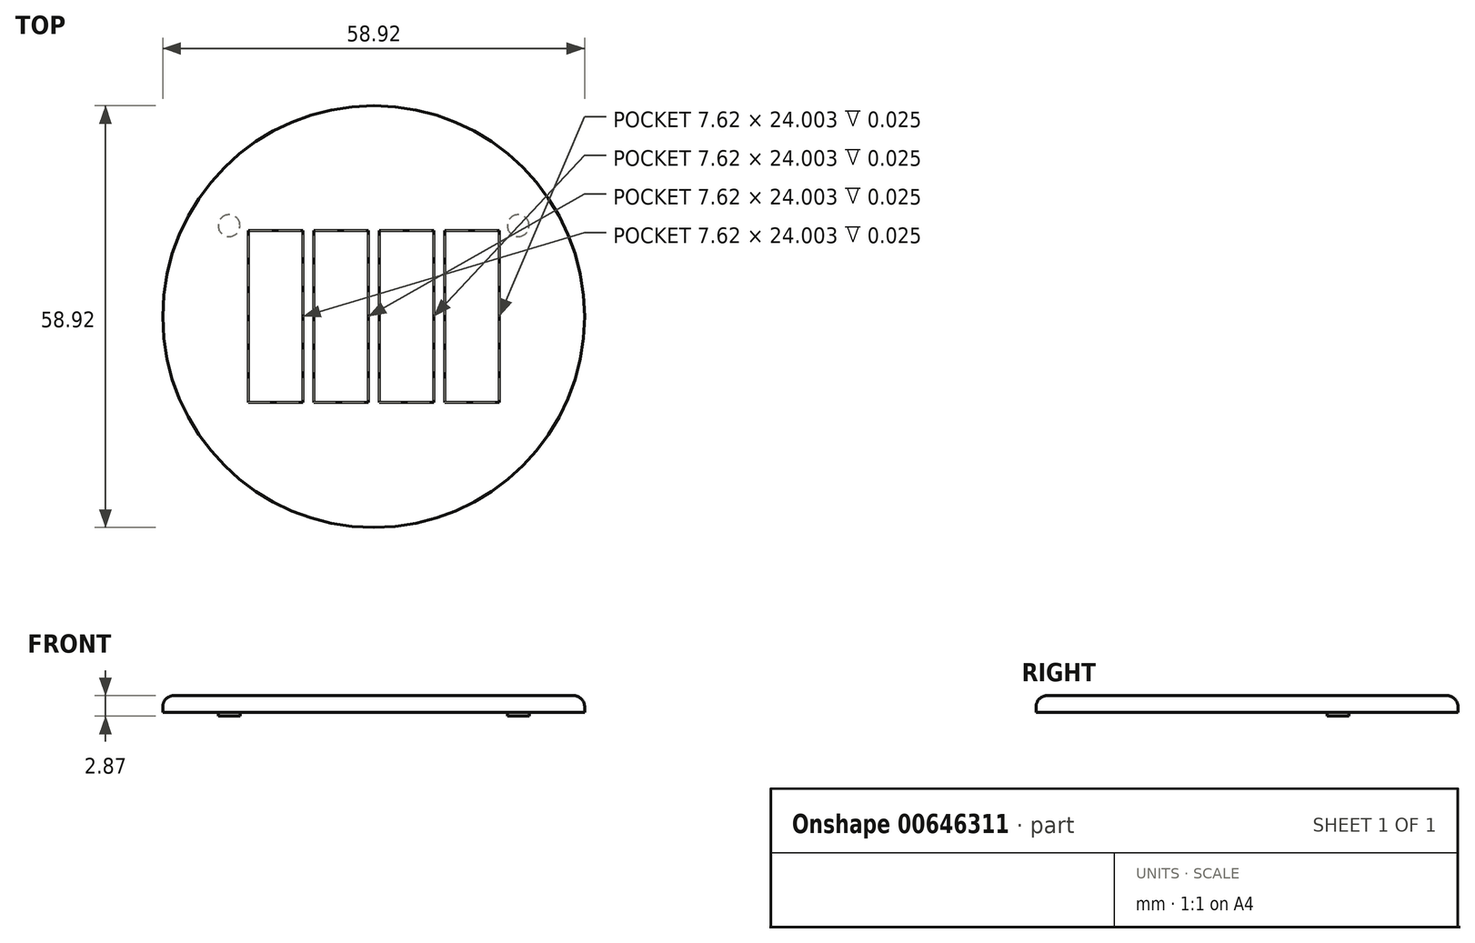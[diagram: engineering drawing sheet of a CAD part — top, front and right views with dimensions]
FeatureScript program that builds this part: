
annotation { "Feature Type Name" : "Feature", "Feature Type Description" : "" }
export const myFeature = defineFeature(function(context is Context, id is Id, definition is map)
    precondition{}
    {
        {
            var Q0;
            Q0=qCreatedBy(makeId("Top.planeOp"),FACE);
            var sketch = newSketch(context, id + "F0", { "sketchPlane" : qUnion([Q0])});
            skCircle(sketch, "E0", {"center": v(0, 0) * mm, "radius": 29.46 * mm});
            skSolve(sketch);
        }
        {
            var Q0;
            Q0 = qSketchRegion(id + "F0", true);
            extrude(context, id + "F1", {"entities" : qUnion([Q0]), "depth" : 2.36 * mm, "offsetDistance" : 25.4 * mm});
        }
        {
            var Q0;
            Q0=makeQuery(id+"F1.opExtrude","CAP_EDGE",EDGE,{"disambiguationData":[OSD([sQuery(id+"F0.wireOp",EDGE,"E0")])],"isStart":false});
            fillet(context, id + "F2", {"entities" : qUnion([Q0]), "radius" : 1.52 * mm, "tangentPropagation" : true, "allowEdgeOverflow" : false});
        }
        {
            var Q0;
            Q0=makeQuery(id+"F1.opExtrude","CAP_FACE",FACE,{"disambiguationData":[OSD([sQuery(id+"F0.wireOp",EDGE,"E0")])],"isStart":false});
            var sketch = newSketch(context, id + "F3", { "sketchPlane" : qUnion([Q0])});
            skLineSegment(sketch, "E1.bottom", {"start": v(-17.53, 12) * mm, "end": v(-9.9, 12) * mm});
            skLineSegment(sketch, "E1.top", {"start": v(-17.53, -12) * mm, "end": v(-9.9, -12) * mm});
            skLineSegment(sketch, "E1.left", {"start": v(-17.53, 12) * mm, "end": v(-17.53, -12) * mm});
            skLineSegment(sketch, "E1.right", {"start": v(-9.9, 12) * mm, "end": v(-9.9, -12) * mm});
            skLineSegment(sketch, "E2.1.0.0", {"start": v(-8.38, 12) * mm, "end": v(-0.76, 12) * mm});
            skLineSegment(sketch, "E2.1.0.1", {"start": v(-8.38, -12) * mm, "end": v(-0.76, -12) * mm});
            skLineSegment(sketch, "E2.1.0.2", {"start": v(-8.38, 12) * mm, "end": v(-8.38, -12) * mm});
            skLineSegment(sketch, "E2.1.0.3", {"start": v(-0.76, 12) * mm, "end": v(-0.76, -12) * mm});
            skLineSegment(sketch, "E2.2.0.0", {"start": v(0.76, 12) * mm, "end": v(8.38, 12) * mm});
            skLineSegment(sketch, "E2.2.0.1", {"start": v(0.76, -12) * mm, "end": v(8.38, -12) * mm});
            skLineSegment(sketch, "E2.2.0.2", {"start": v(0.76, 12) * mm, "end": v(0.76, -12) * mm});
            skLineSegment(sketch, "E2.2.0.3", {"start": v(8.38, 12) * mm, "end": v(8.38, -12) * mm});
            skLineSegment(sketch, "E2.3.0.0", {"start": v(9.9, 12) * mm, "end": v(17.53, 12) * mm});
            skLineSegment(sketch, "E2.3.0.1", {"start": v(9.9, -12) * mm, "end": v(17.53, -12) * mm});
            skLineSegment(sketch, "E2.3.0.2", {"start": v(9.9, 12) * mm, "end": v(9.9, -12) * mm});
            skLineSegment(sketch, "E2.3.0.3", {"start": v(17.53, 12) * mm, "end": v(17.53, -12) * mm});
            skLineSegment(sketch, "E2.direction1", {"start": v(-17.53, -12) * mm, "end": v(-8.38, -12) * mm, "construction": true});
            skSolve(sketch);
        }
        {
            var Q0;
            Q0 = qSketchRegion(id + "F3", true);
            extrude(context, id + "F4", {"entities" : qUnion([Q0]), "operationType" : NewBodyOperationType.REMOVE, "oppositeDirection" : true, "depth" : 0.03 * mm, "offsetDistance" : 25.4 * mm});
        }
        {
            var Q0;
            Q0=makeQuery(id+"F1.opExtrude","CAP_FACE",FACE,{"disambiguationData":[OSD([sQuery(id+"F0.wireOp",EDGE,"E0")])],"isStart":true});
            var sketch = newSketch(context, id + "F5", { "sketchPlane" : qUnion([Q0])});
            skCircle(sketch, "E3", {"center": v(-20.2, -12.7) * mm, "radius": 1.52 * mm});
            skCircle(sketch, "E4", {"center": v(20.2, -12.7) * mm, "radius": 1.52 * mm});
            skSolve(sketch);
        }
        {
            var Q0;
            Q0 = qSketchRegion(id + "F5", true);
            extrude(context, id + "F6", {"entities" : qUnion([Q0]), "operationType" : NewBodyOperationType.ADD, "depth" : 0.5 * mm, "offsetDistance" : 25.4 * mm});
        }
    });
